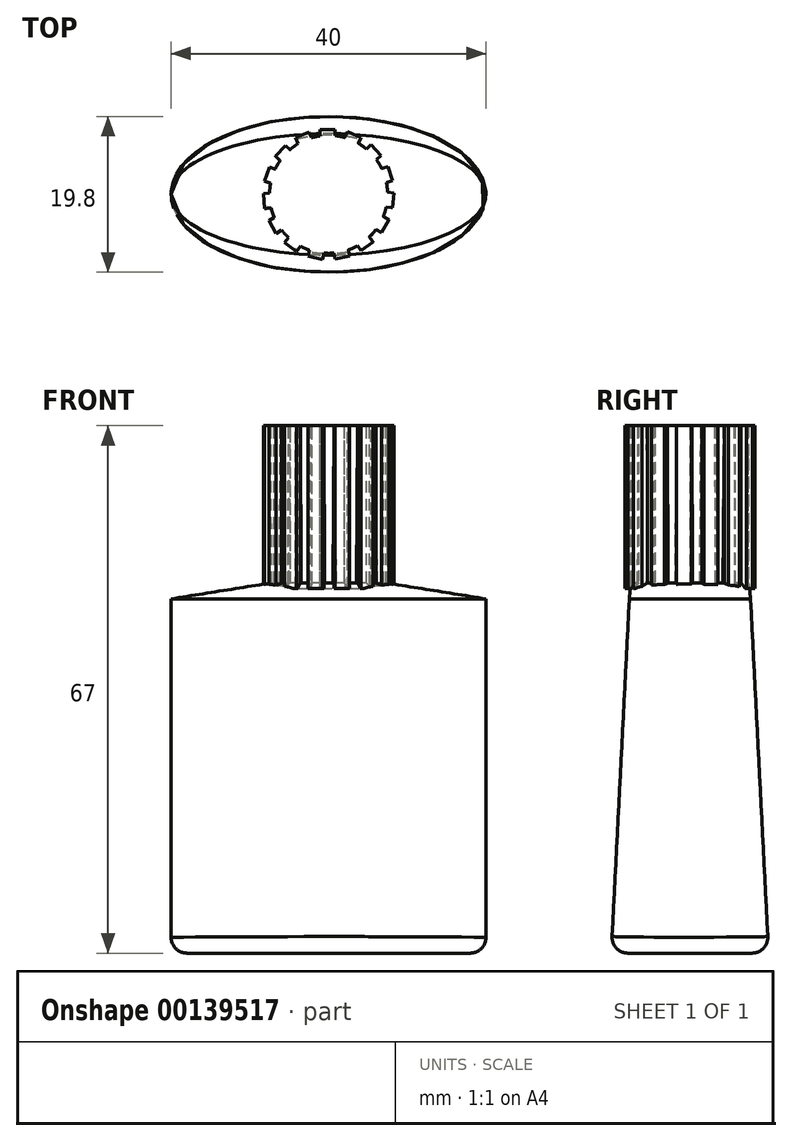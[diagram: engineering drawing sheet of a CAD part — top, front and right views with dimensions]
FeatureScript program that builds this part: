
annotation { "Feature Type Name" : "Feature", "Feature Type Description" : "" }
export const myFeature = defineFeature(function(context is Context, id is Id, definition is map)
    precondition{}
    {
        {
            var Q0;
            Q0=qCreatedBy(makeId("Top.planeOp"),FACE);
            cPlane(context, id + "F0", {"entities" : qUnion([Q0]), "cplaneType" : CPlaneType.OFFSET, "offset" : 45 * mm, "width" : 150 * mm, "height" : 150 * mm});
        }
        {
            var Q0;
            Q0=qCreatedBy(id+"F0.planeOp",FACE);
            cPlane(context, id + "F1", {"entities" : qUnion([Q0]), "cplaneType" : CPlaneType.OFFSET, "offset" : 22 * mm, "width" : 150 * mm, "height" : 150 * mm});
        }
        {
            var Q0;
            Q0=qCreatedBy(makeId("Top.planeOp"),FACE);
            var sketch = newSketch(context, id + "F2", { "sketchPlane" : qUnion([Q0])});
            skEllipse(sketch, "E0", {"center": v(0, 0) * mm, "majorRadius": 20 * mm, "minorRadius": 10 * mm, "majorAxis": v(-1, 0)});
            skSolve(sketch);
        }
        {
            var Q0;
            Q0=qCreatedBy(id+"F0.planeOp",FACE);
            var sketch = newSketch(context, id + "F3", { "sketchPlane" : qUnion([Q0])});
            skEllipse(sketch, "E1", {"center": v(0, 0) * mm, "majorRadius": 20 * mm, "minorRadius": 7.7 * mm, "majorAxis": v(-1, 0)});
            skSolve(sketch);
        }
        {
            var Q0;
            Q0=makeQuery(id+"F2.imprint","IMPRINT",FACE,{"disambiguationData":[TD([[makeQuery(id+"F2.imprint","IMPRINT",EDGE,{"derivedFrom":sQuery(id+"F2.wireOp",EDGE,"E0")}),1.0]])]});
            var Q1;
            Q1=makeQuery(id+"F3.imprint","IMPRINT",FACE,{"disambiguationData":[TD([[makeQuery(id+"F3.imprint","IMPRINT",EDGE,{"derivedFrom":sQuery(id+"F3.wireOp",EDGE,"E1")}),1.0]])]});
            loft(context, id + "F4", {"sheetProfilesArray" : [{ "sheetProfileEntities" : qUnion([Q0]) }, { "sheetProfileEntities" : qUnion([Q1]) }]});
        }
        {
            var Q0;
            Q0=qCreatedBy(id+"F1.planeOp",FACE);
            var sketch = newSketch(context, id + "F5", { "sketchPlane" : qUnion([Q0])});
            skCircle(sketch, "E2", {"center": v(0, 0) * mm, "radius": 7.5 * mm});
            skLineSegment(sketch, "E3.bottom", {"start": v(-1.08, 7.42) * mm, "end": v(0.8, 7.42) * mm});
            skLineSegment(sketch, "E3.top", {"start": v(-1.08, 8.24) * mm, "end": v(0.8, 8.24) * mm});
            skLineSegment(sketch, "E3.left", {"start": v(-1.08, 7.42) * mm, "end": v(-1.08, 8.24) * mm});
            skLineSegment(sketch, "E3.right", {"start": v(0.8, 7.42) * mm, "end": v(0.8, 8.24) * mm});
            skLineSegment(sketch, "E4.1.0", {"start": v(2.38, 7.96) * mm, "end": v(4.1, 7.2) * mm});
            skLineSegment(sketch, "E4.1.1", {"start": v(2.04, 7.22) * mm, "end": v(3.76, 6.45) * mm});
            skLineSegment(sketch, "E4.1.2", {"start": v(3.76, 6.45) * mm, "end": v(4.1, 7.2) * mm});
            skLineSegment(sketch, "E4.1.3", {"start": v(2.04, 7.22) * mm, "end": v(2.38, 7.96) * mm});
            skLineSegment(sketch, "E4.2.0", {"start": v(5.42, 6.3) * mm, "end": v(6.67, 4.9) * mm});
            skLineSegment(sketch, "E4.2.1", {"start": v(4.81, 5.75) * mm, "end": v(6.06, 4.35) * mm});
            skLineSegment(sketch, "E4.2.2", {"start": v(6.06, 4.35) * mm, "end": v(6.67, 4.9) * mm});
            skLineSegment(sketch, "E4.2.3", {"start": v(4.81, 5.75) * mm, "end": v(5.42, 6.3) * mm});
            skLineSegment(sketch, "E4.3.0", {"start": v(7.52, 3.54) * mm, "end": v(8.1, 1.75) * mm});
            skLineSegment(sketch, "E4.3.1", {"start": v(6.74, 3.3) * mm, "end": v(7.31, 1.5) * mm});
            skLineSegment(sketch, "E4.3.2", {"start": v(7.31, 1.5) * mm, "end": v(8.1, 1.75) * mm});
            skLineSegment(sketch, "E4.3.3", {"start": v(6.74, 3.3) * mm, "end": v(7.52, 3.54) * mm});
            skLineSegment(sketch, "E4.4.0", {"start": v(8.3, 0.16) * mm, "end": v(8.1, -1.7) * mm});
            skLineSegment(sketch, "E4.4.1", {"start": v(7.5, 0.25) * mm, "end": v(7.29, -1.61) * mm});
            skLineSegment(sketch, "E4.4.2", {"start": v(7.29, -1.61) * mm, "end": v(8.1, -1.7) * mm});
            skLineSegment(sketch, "E4.4.3", {"start": v(7.5, 0.25) * mm, "end": v(8.3, 0.16) * mm});
            skLineSegment(sketch, "E4.5.0", {"start": v(7.65, -3.24) * mm, "end": v(6.7, -4.86) * mm});
            skLineSegment(sketch, "E4.5.1", {"start": v(6.95, -2.83) * mm, "end": v(6, -4.45) * mm});
            skLineSegment(sketch, "E4.5.2", {"start": v(6, -4.45) * mm, "end": v(6.7, -4.86) * mm});
            skLineSegment(sketch, "E4.5.3", {"start": v(6.95, -2.83) * mm, "end": v(7.65, -3.24) * mm});
            skLineSegment(sketch, "E4.6.0", {"start": v(5.66, -6.08) * mm, "end": v(4.14, -7.17) * mm});
            skLineSegment(sketch, "E4.6.1", {"start": v(5.19, -5.42) * mm, "end": v(3.66, -6.5) * mm});
            skLineSegment(sketch, "E4.6.2", {"start": v(3.66, -6.5) * mm, "end": v(4.14, -7.17) * mm});
            skLineSegment(sketch, "E4.6.3", {"start": v(5.19, -5.42) * mm, "end": v(5.66, -6.08) * mm});
            skLineSegment(sketch, "E4.7.0", {"start": v(2.7, -7.86) * mm, "end": v(0.85, -8.24) * mm});
            skLineSegment(sketch, "E4.7.1", {"start": v(2.53, -7.06) * mm, "end": v(0.69, -7.43) * mm});
            skLineSegment(sketch, "E4.7.2", {"start": v(0.69, -7.43) * mm, "end": v(0.85, -8.24) * mm});
            skLineSegment(sketch, "E4.7.3", {"start": v(2.53, -7.06) * mm, "end": v(2.7, -7.86) * mm});
            skLineSegment(sketch, "E4.8.0", {"start": v(-0.75, -8.28) * mm, "end": v(-2.59, -7.87) * mm});
            skLineSegment(sketch, "E4.8.1", {"start": v(-0.57, -7.48) * mm, "end": v(-2.4, -7.07) * mm});
            skLineSegment(sketch, "E4.8.2", {"start": v(-2.4, -7.07) * mm, "end": v(-2.59, -7.87) * mm});
            skLineSegment(sketch, "E4.8.3", {"start": v(-0.57, -7.48) * mm, "end": v(-0.75, -8.28) * mm});
            skLineSegment(sketch, "E4.9.0", {"start": v(-4.07, -7.25) * mm, "end": v(-5.57, -6.13) * mm});
            skLineSegment(sketch, "E4.9.1", {"start": v(-3.58, -6.6) * mm, "end": v(-5.08, -5.47) * mm});
            skLineSegment(sketch, "E4.9.2", {"start": v(-5.08, -5.47) * mm, "end": v(-5.57, -6.13) * mm});
            skLineSegment(sketch, "E4.9.3", {"start": v(-3.58, -6.6) * mm, "end": v(-4.07, -7.25) * mm});
            skLineSegment(sketch, "E4.10.0", {"start": v(-6.67, -4.96) * mm, "end": v(-7.59, -3.32) * mm});
            skLineSegment(sketch, "E4.10.1", {"start": v(-5.95, -4.56) * mm, "end": v(-6.87, -2.92) * mm});
            skLineSegment(sketch, "E4.10.2", {"start": v(-6.87, -2.92) * mm, "end": v(-7.59, -3.32) * mm});
            skLineSegment(sketch, "E4.10.3", {"start": v(-5.95, -4.56) * mm, "end": v(-6.67, -4.96) * mm});
            skLineSegment(sketch, "E4.11.0", {"start": v(-8.11, -1.8) * mm, "end": v(-8.28, 0.06) * mm});
            skLineSegment(sketch, "E4.11.1", {"start": v(-7.3, -1.73) * mm, "end": v(-7.46, 0.14) * mm});
            skLineSegment(sketch, "E4.11.2", {"start": v(-7.46, 0.14) * mm, "end": v(-8.28, 0.06) * mm});
            skLineSegment(sketch, "E4.11.3", {"start": v(-7.3, -1.73) * mm, "end": v(-8.11, -1.8) * mm});
            skLineSegment(sketch, "E4.12.0", {"start": v(-8.14, 1.66) * mm, "end": v(-7.53, 3.44) * mm});
            skLineSegment(sketch, "E4.12.1", {"start": v(-7.37, 1.4) * mm, "end": v(-6.76, 3.17) * mm});
            skLineSegment(sketch, "E4.12.2", {"start": v(-6.76, 3.17) * mm, "end": v(-7.53, 3.44) * mm});
            skLineSegment(sketch, "E4.12.3", {"start": v(-7.37, 1.4) * mm, "end": v(-8.14, 1.66) * mm});
            skLineSegment(sketch, "E4.13.0", {"start": v(-6.76, 4.84) * mm, "end": v(-5.47, 6.21) * mm});
            skLineSegment(sketch, "E4.13.1", {"start": v(-6.16, 4.28) * mm, "end": v(-4.88, 5.65) * mm});
            skLineSegment(sketch, "E4.13.2", {"start": v(-4.88, 5.65) * mm, "end": v(-5.47, 6.21) * mm});
            skLineSegment(sketch, "E4.13.3", {"start": v(-6.16, 4.28) * mm, "end": v(-6.76, 4.84) * mm});
            skLineSegment(sketch, "E4.14.0", {"start": v(-4.2, 7.18) * mm, "end": v(-2.46, 7.9) * mm});
            skLineSegment(sketch, "E4.14.1", {"start": v(-3.88, 6.42) * mm, "end": v(-2.14, 7.15) * mm});
            skLineSegment(sketch, "E4.14.2", {"start": v(-2.14, 7.15) * mm, "end": v(-2.46, 7.9) * mm});
            skLineSegment(sketch, "E4.14.3", {"start": v(-3.88, 6.42) * mm, "end": v(-4.2, 7.18) * mm});
            skLineSegment(sketch, "E4.anchor1", {"start": v(0, 0) * mm, "end": v(-1.08, 8.24) * mm, "construction": true});
            skLineSegment(sketch, "E4.anchor2", {"start": v(0, 0) * mm, "end": v(-4.2, 7.18) * mm, "construction": true});
            skSolve(sketch);
        }
        {
            var Q0;
            Q0=qCreatedBy(id+"F0.planeOp",FACE);
            cPlane(context, id + "F6", {"entities" : qUnion([Q0]), "cplaneType" : CPlaneType.OFFSET, "offset" : 2 * mm, "width" : 150 * mm, "height" : 150 * mm});
        }
        {
            var Q0;
            Q0=qCreatedBy(id+"F6.planeOp",FACE);
            var sketch = newSketch(context, id + "F7", { "sketchPlane" : qUnion([Q0])});
            skCircle(sketch, "E5", {"center": v(0, 0) * mm, "radius": 7.5 * mm});
            skSolve(sketch);
        }
        {
            var Q1;
            Q1=makeQuery(id+"F4.opLoft","CAP_FACE",FACE,{"disambiguationData":[OSD([makeQuery(id+"F3.imprint","IMPRINT",FACE,{"disambiguationData":[TD([[makeQuery(id+"F3.imprint","IMPRINT",EDGE,{"derivedFrom":sQuery(id+"F3.wireOp",EDGE,"E1")}),1.0]])]})])],"isStart":true});
            var Q2;
            Q2=makeQuery(id+"F7.imprint","IMPRINT",FACE,{"disambiguationData":[TD([[makeQuery(id+"F7.imprint","IMPRINT",EDGE,{"derivedFrom":sQuery(id+"F7.wireOp",EDGE,"E5")}),1.0]])]});
            loft(context, id + "F8", {"operationType" : NewBodyOperationType.ADD, "sheetProfilesArray" : [{ "sheetProfileEntities" : qUnion([Q1]) }, { "sheetProfileEntities" : qUnion([Q2]) }]});
        }
        {
            var Q1;
            Q1=makeQuery(id+"F8.opLoft","CAP_FACE",FACE,{"disambiguationData":[OSD([makeQuery(id+"F7.imprint","IMPRINT",FACE,{"disambiguationData":[TD([[makeQuery(id+"F7.imprint","IMPRINT",EDGE,{"derivedFrom":sQuery(id+"F7.wireOp",EDGE,"E5")}),1.0]])]})])],"isStart":true});
            var Q2;
            Q2=makeQuery(id+"F5.imprint","IMPRINT",FACE,{"disambiguationData":[TD([[makeQuery(id+"F5.imprint","IMPRINT",EDGE,{"derivedFrom":sQuery(id+"F5.wireOp",EDGE,"E2")}),1.0]])]});
            loft(context, id + "F9", {"operationType" : NewBodyOperationType.ADD, "sheetProfilesArray" : [{ "sheetProfileEntities" : qUnion([Q1]) }, { "sheetProfileEntities" : qUnion([Q2]) }]});
        }
        {
            var Q0;
            Q0=makeQuery(id+"F4.opLoft","CAP_FACE",FACE,{"disambiguationData":[OSD([makeQuery(id+"F2.imprint","IMPRINT",FACE,{"disambiguationData":[TD([[makeQuery(id+"F2.imprint","IMPRINT",EDGE,{"derivedFrom":sQuery(id+"F2.wireOp",EDGE,"E0")}),1.0]])]})])],"isStart":true});
            fillet(context, id + "F10", {"entities" : qUnion([Q0]), "radius" : 2 * mm, "tangentPropagation" : true, "allowEdgeOverflow" : false});
        }
        {
            var Q0;
            Q0 = qSketchRegion(id + "F5", true);
            extrude(context, id + "F11", {"entities" : qUnion([Q0]), "operationType" : NewBodyOperationType.ADD, "oppositeDirection" : true, "depth" : 20.68 * mm});
        }
    });
